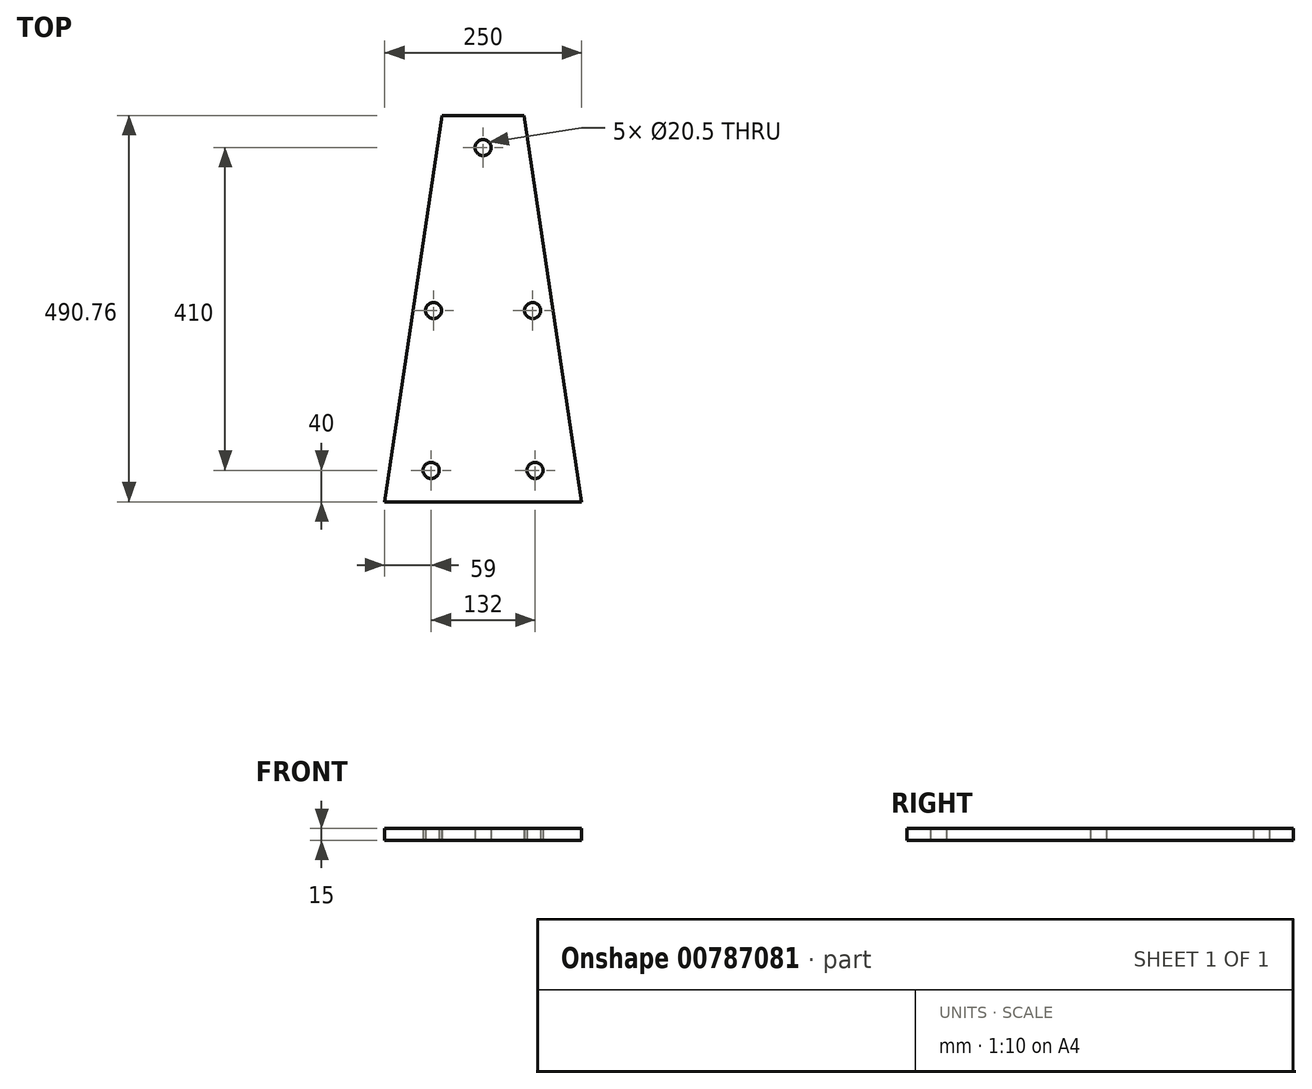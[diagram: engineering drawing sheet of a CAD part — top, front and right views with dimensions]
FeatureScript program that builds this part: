
annotation { "Feature Type Name" : "Feature", "Feature Type Description" : "" }
export const myFeature = defineFeature(function(context is Context, id is Id, definition is map)
    precondition{}
    {
        {
            var Q0;
            Q0=qCreatedBy(makeId("Top.planeOp"),FACE);
            var sketch = newSketch(context, id + "F0", { "sketchPlane" : qUnion([Q0])});
            skLineSegment(sketch, "E0", {"start": v(0, 0) * mm, "end": v(250, 0) * mm});
            skLineSegment(sketch, "E1", {"start": v(250, 0) * mm, "end": v(125, 840.76) * mm});
            skLineSegment(sketch, "E2", {"start": v(125, 840.76) * mm, "end": v(0, 0) * mm});
            skLineSegment(sketch, "E3", {"start": v(125, 840.76) * mm, "end": v(125, 0) * mm});
            skLineSegment(sketch, "E4", {"start": v(72.96, 490.76) * mm, "end": v(177.04, 490.76) * mm});
            skSolve(sketch);
        }
        {
            var Q0;
            Q0=makeQuery(id+"F0.imprint","IMPRINT",FACE,{"disambiguationData":[TD([[makeQuery(id+"F0.imprint","IMPRINT",EDGE,{"derivedFrom":sQuery(id+"F0.wireOp",EDGE,"E0")}),1.0]])]});
            extrude(context, id + "F1", {"entities" : qUnion([Q0]), "depth" : 15 * mm, "offsetDistance" : 25 * mm});
        }
        {
            var Q0;
            Q0=qCreatedBy(makeId("Top.planeOp"),FACE);
            var sketch = newSketch(context, id + "F2", { "sketchPlane" : qUnion([Q0])});
            skCircle(sketch, "E5", {"center": v(59, 40) * mm, "radius": 25.5 * mm});
            skCircle(sketch, "E6", {"center": v(62, 243) * mm, "radius": 25.5 * mm});
            skCircle(sketch, "E7", {"center": v(191, 40) * mm, "radius": 25.5 * mm});
            skCircle(sketch, "E8", {"center": v(188, 243) * mm, "radius": 25.5 * mm});
            skCircle(sketch, "E9", {"center": v(125, 450) * mm, "radius": 25.5 * mm});
            skSolve(sketch);
        }
        {
            var Q0;
            Q0=sQuery(id+"F2.wireOp",VERTEX,"E9.center");
            var Q1;
            Q1=sQuery(id+"F2.wireOp",VERTEX,"E6.center");
            var Q2;
            Q2=sQuery(id+"F2.wireOp",VERTEX,"E8.center");
            var Q3;
            Q3=sQuery(id+"F2.wireOp",VERTEX,"E7.center");
            var Q4;
            Q4=sQuery(id+"F2.wireOp",VERTEX,"E5.center");
            var Q5;
            Q5=makeQuery(id+"F1.opExtrude","SWEPT_BODY",BODY,{"disambiguationData":[OSD([sQuery(id+"F0.wireOp",EDGE,"E0"),sQuery(id+"F0.wireOp",EDGE,"E1"),sQuery(id+"F0.wireOp",EDGE,"E2")])]});
            hole(context, id + "F3", {"style" : HoleStyle.SIMPLE, "endStyle" : HoleEndStyle.THROUGH, "oppositeDirection" : true, "holeDiameter" : 20.5 * mm, "majorDiameter" : 5 * mm, "isTappedThrough" : true, "tappedDepth" : 12 * mm, "tapClearance" : 3, "locations" : qUnion([Q0, Q1, Q2, Q3, Q4]), "scope" : qUnion([Q5])});
        }
    });
